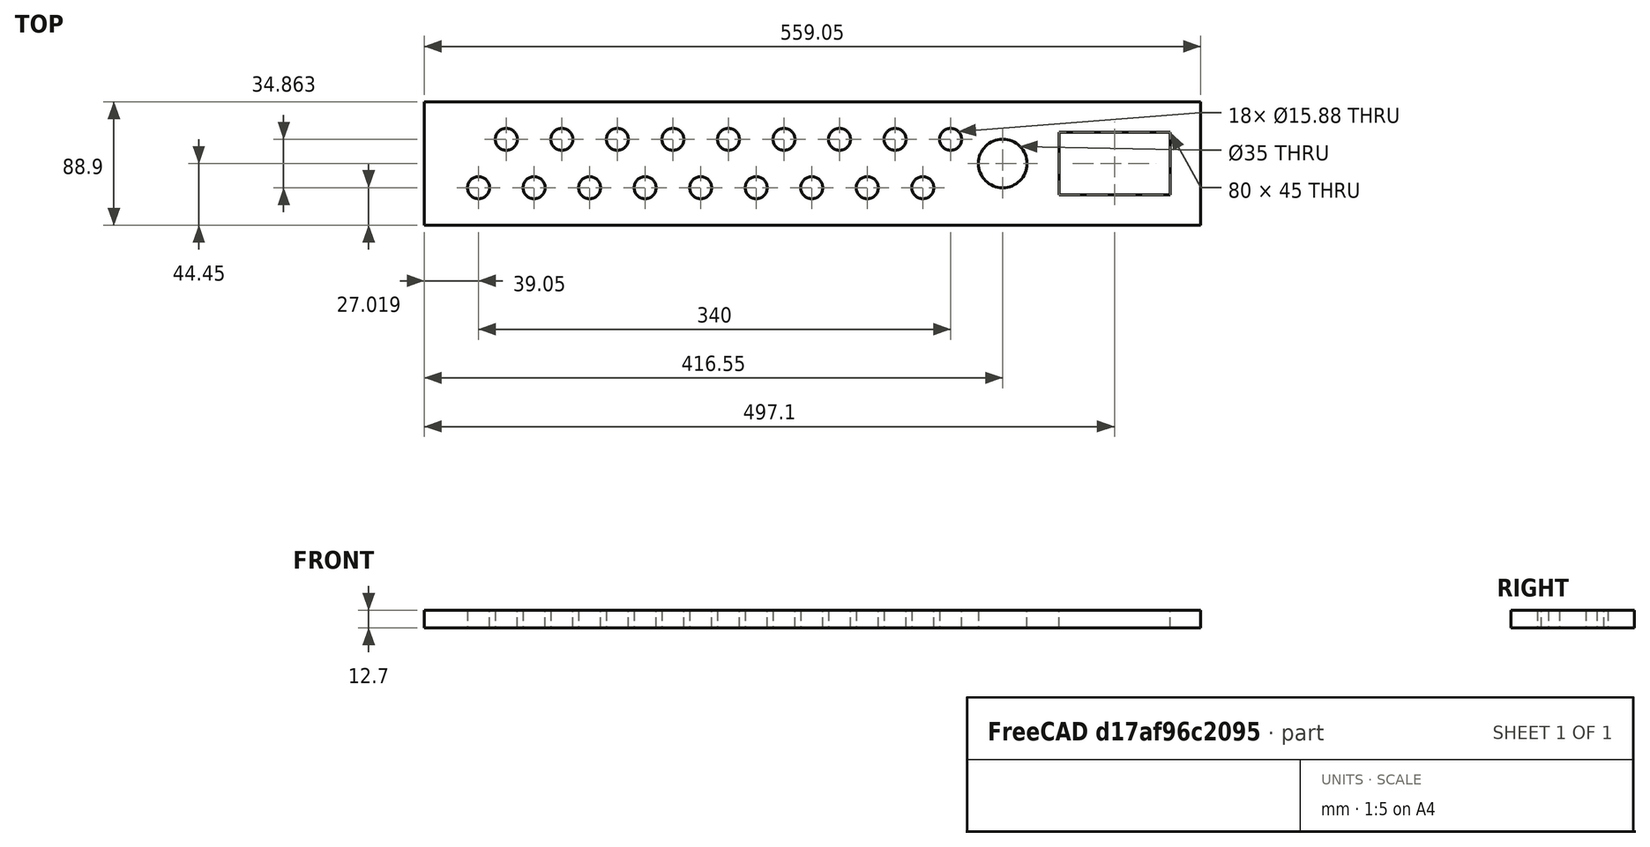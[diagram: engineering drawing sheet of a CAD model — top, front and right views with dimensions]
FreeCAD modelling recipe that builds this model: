
FCSTD DOCUMENT  (FreeCAD 0.19R24291 (Git))
Label: top3
License: All rights reserved
LicenseURL: http://en.wikipedia.org/wiki/All_rights_reserved
objects: TechDraw::DrawViewDimension×14, Sketcher::SketchObject×1, PartDesign::Pad×1, PartDesign::Body×1, TechDraw::DrawSVGTemplate×1, TechDraw::DrawViewPart×1, TechDraw::DrawPage×1
note: 4 computed .brp shape members not serialized (recipe doc carries the construction recipe); baked Part::Feature solids carry a one-line shape summary decoded from their .brp

FEATURE [Sketcher::SketchObject] Sketch
  FullyConstrained = true
  MapMode = 5
  Support = -> [XY_Plane]
  expr: Constraints[34] = (3.5 * 25.4 - 2 * 5 / 8 * 25.4) / 3 + 5 / 8 * 25.5 / 2
  expr: Constraints[0] = 5 / 8 * 25.4
  expr: Constraints[26] = 3.5 * 25.4
  expr: Constraints[38] = 20 + 20
  expr: Constraints[53] = (3.5 * 25.4 - 2 * 5 / 8 * 25.4) / 3 + 5 / 8 * 25.5 / 2
  expr: Constraints[103] = 3 / 4 * 25.4
  sketch-geometry (35):
    g0: Circle CenterX=20 CenterY=27.0187 CenterZ=0 NormalX=0 NormalY=0 NormalZ=1 AngleXU=0 Radius=7.9375
    g1: LineSegment StartX=-2e-16 StartY=27.0187 StartZ=0 EndX=380 EndY=27.0187 EndZ=0
    g2: Circle CenterX=60 CenterY=27.0187 CenterZ=0 NormalX=0 NormalY=0 NormalZ=1 AngleXU=0 Radius=7.9375
    g3: Circle CenterX=397.5 CenterY=44.45 CenterZ=0 NormalX=0 NormalY=0 NormalZ=1 AngleXU=0 Radius=17.5
    g4: LineSegment StartX=438.05 StartY=66.95 StartZ=0 EndX=518.05 EndY=66.95 EndZ=0
    g5: LineSegment StartX=518.05 StartY=66.95 StartZ=0 EndX=518.05 EndY=21.95 EndZ=0
    g6: LineSegment StartX=518.05 StartY=21.95 StartZ=0 EndX=438.05 EndY=21.95 EndZ=0
    g7: LineSegment StartX=438.05 StartY=21.95 StartZ=0 EndX=438.05 EndY=66.95 EndZ=0
    g8: LineSegment StartX=0 StartY=88.9 StartZ=0 EndX=540 EndY=88.9 EndZ=0
    g9: LineSegment StartX=540 StartY=88.9 StartZ=0 EndX=540 EndY=0 EndZ=0
    g10: LineSegment StartX=540 StartY=0 StartZ=0 EndX=0 EndY=0 EndZ=0
    g11: LineSegment StartX=0 StartY=0 StartZ=0 EndX=0 EndY=88.9 EndZ=0
    g12: LineSegment StartX=540 StartY=44.45 StartZ=0 EndX=0 EndY=44.45 EndZ=0
    g13: GeomPoint X=518.05 Y=44.45 Z=0
    g14: LineSegment StartX=0 StartY=61.8812 StartZ=0 EndX=380 EndY=61.8812 EndZ=0
    g15: Circle CenterX=40 CenterY=61.8812 CenterZ=0 NormalX=0 NormalY=0 NormalZ=1 AngleXU=0 Radius=7.9375
    g16: Circle CenterX=100 CenterY=27.0187 CenterZ=0 NormalX=0 NormalY=0 NormalZ=1 AngleXU=0 Radius=7.9375
    g17: Circle CenterX=140 CenterY=27.0187 CenterZ=0 NormalX=0 NormalY=0 NormalZ=1 AngleXU=0 Radius=7.9375
    g18: Circle CenterX=180 CenterY=27.0187 CenterZ=0 NormalX=0 NormalY=0 NormalZ=1 AngleXU=0 Radius=7.9375
    g19: Circle CenterX=220 CenterY=27.0187 CenterZ=0 NormalX=0 NormalY=0 NormalZ=1 AngleXU=0 Radius=7.9375
    g20: Circle CenterX=260 CenterY=27.0187 CenterZ=0 NormalX=0 NormalY=0 NormalZ=1 AngleXU=0 Radius=7.9375
    g21: Circle CenterX=300 CenterY=27.0187 CenterZ=0 NormalX=0 NormalY=0 NormalZ=1 AngleXU=0 Radius=7.9375
    g22: Circle CenterX=340 CenterY=27.0187 CenterZ=0 NormalX=0 NormalY=0 NormalZ=1 AngleXU=0 Radius=7.9375
    g23: Circle CenterX=80 CenterY=61.8812 CenterZ=0 NormalX=0 NormalY=0 NormalZ=1 AngleXU=0 Radius=7.9375
    g24: Circle CenterX=120 CenterY=61.8812 CenterZ=0 NormalX=0 NormalY=0 NormalZ=1 AngleXU=0 Radius=7.9375
    g25: Circle CenterX=160 CenterY=61.8812 CenterZ=0 NormalX=0 NormalY=0 NormalZ=1 AngleXU=0 Radius=7.9375
    g26: Circle CenterX=200 CenterY=61.8812 CenterZ=0 NormalX=0 NormalY=0 NormalZ=1 AngleXU=0 Radius=7.9375
    g27: Circle CenterX=240 CenterY=61.8812 CenterZ=0 NormalX=0 NormalY=0 NormalZ=1 AngleXU=0 Radius=7.9375
    g28: Circle CenterX=280 CenterY=61.8812 CenterZ=0 NormalX=0 NormalY=0 NormalZ=1 AngleXU=0 Radius=7.9375
    g29: Circle CenterX=320 CenterY=61.8812 CenterZ=0 NormalX=0 NormalY=0 NormalZ=1 AngleXU=0 Radius=7.9375
    g30: Circle CenterX=360 CenterY=61.8812 CenterZ=0 NormalX=0 NormalY=0 NormalZ=1 AngleXU=0 Radius=7.9375
    g31: LineSegment StartX=380 StartY=0 StartZ=0 EndX=380 EndY=88.9 EndZ=0
    g32: LineSegment StartX=0 StartY=0 StartZ=0 EndX=-19.05 EndY=0 EndZ=0
    g33: LineSegment StartX=-19.05 StartY=0 StartZ=0 EndX=-19.05 EndY=88.9 EndZ=0
    g34: LineSegment StartX=-19.05 StartY=88.9 StartZ=0 EndX=0 EndY=88.9 EndZ=0
  constraints (105):
    c: Diameter(g0) = 15.875
    c: Horizontal(g1)
    c: PointOnObject(g0,g1)
    c: DistanceX(g1,g0) = 20
    c: Equal(g0,g2) = 15.875
    c: PointOnObject(g2,g1)
    c: DistanceX(g0,g2) = 40
    c: Diameter(g3) = 35
    c: Coincident(g4,g5)
    c: Coincident(g5,g6)
    c: Coincident(g6,g7)
    c: Coincident(g7,g4)
    c: Horizontal(g4)
    c: Horizontal(g6)
    c: Vertical(g5)
    c: Vertical(g7)
    c: DistanceX(g6,g6) = 80
    c: DistanceY(g5,g5) = 45
    c: Coincident(g8,g9)
    c: Coincident(g9,g10)
    c: Coincident(g10,g11)
    c: Coincident(g11,g8)
    c: Horizontal(g8)
    c: Horizontal(g10)
    c: Vertical(g9)
    c: Vertical(g11)
    c: DistanceY(g11,g11) = 88.9
    c: Coincident(g10,g-1)
    c: Horizontal(g12)
    c: Symmetric(g8,g9,g12)
    c: Symmetric(g4,g5,g13)
    c: PointOnObject(g13,g12)
    c: PointOnObject(g3,g12)
    c: PointOnObject(g1,g11)
    c: DistanceY(g10,g1) = 27.0187
    c: Horizontal(g14)
    c: PointOnObject(g14,g11)
    c: PointOnObject(g15,g14)
    c: DistanceX(g14,g15) = 40
    c: Equal(g0,g16) = 15.875
    c: PointOnObject(g16,g1)
    c: Equal(g0,g17) = 15.875
    c: PointOnObject(g17,g1)
    c: Equal(g0,g18) = 15.875
    c: PointOnObject(g18,g1)
    c: Equal(g0,g19) = 15.875
    c: PointOnObject(g19,g1)
    c: Equal(g0,g20) = 15.875
    c: PointOnObject(g20,g1)
    c: Equal(g0,g21) = 15.875
    c: PointOnObject(g21,g1)
    c: Equal(g0,g22) = 15.875
    c: PointOnObject(g22,g1)
    c: DistanceY(g14,g8) = 27.0187
    c: Equal(g0,g23) = 15.875
    c: PointOnObject(g23,g14)
    c: Equal(g0,g24) = 15.875
    c: PointOnObject(g24,g14)
    c: Equal(g0,g25) = 15.875
    c: PointOnObject(g25,g14)
    c: Equal(g0,g26) = 15.875
    c: PointOnObject(g26,g14)
    c: Equal(g0,g27) = 15.875
    c: PointOnObject(g27,g14)
    c: Equal(g0,g28) = 15.875
    c: PointOnObject(g28,g14)
    c: Equal(g0,g29) = 15.875
    c: PointOnObject(g29,g14)
    c: Equal(g0,g30) = 15.875
    c: PointOnObject(g30,g14)
    c: PointOnObject(g31,g10)
    c: PointOnObject(g31,g8)
    c: Vertical(g31)
    c: PointOnObject(g14,g31)
    c: PointOnObject(g1,g31)
    c: DistanceX(g15,g23) = 40
    c: DistanceX(g23,g24) = 40
    c: DistanceX(g24,g25) = 40
    c: DistanceX(g25,g26) = 40
    c: DistanceX(g26,g27) = 40
    c: DistanceX(g27,g28) = 40
    c: DistanceX(g28,g29) = 40
    c: DistanceX(g29,g30) = 40
    c: PointOnObject(g12,g11)
    c: Equal(g15,g0)
    c: DistanceX(g2,g16) = 40
    c: DistanceX(g16,g17) = 40
    c: DistanceX(g17,g18) = 40
    c: DistanceX(g18,g19) = 40
    c: DistanceX(g19,g20) = 40
    c: DistanceX(g20,g21) = 40
    c: DistanceX(g21,g22) = 40
    c: DistanceX(g30,g14) = 20
    c: Tangent(g3,g31)
    c: DistanceY(g4,g8) = 21.95
    c: DistanceX(g13,g12) = 21.95
    c: Coincident(g10,g32)
    c: PointOnObject(g32,g-1)
    c: Coincident(g32,g33)
    c: Vertical(g33)
    c: Coincident(g33,g34)
    c: Coincident(g34,g8)
    c: Horizontal(g34)
    c: DistanceX(g32,g10) = 19.05
    c: DistanceX(g10,g9) = 540
FEATURE [PartDesign::Pad] Pad
  Direction = (1,1,1)
  Length = 12.7
  Length2 = 100
  Profile = -> Sketch
  Type = 0
  expr: Length = 1 / 2 * 25.4
FEATURE [PartDesign::Body] Body
  Group = -> [Sketch,Pad]
  Origin = -> Origin
  Tip = -> Pad
FEATURE [TechDraw::DrawSVGTemplate] Template
  EditableTexts = Designed_by_Name=Designed by Name; Drawing_number=Drawing number; FC-Date=Date; FC-SC=Scale; FC-SH=Sheet; FC-Title=Title; Subtitle=Subtitle; Weight=Weight
  Height = 210
  Orientation = 1
  Width = 297
FEATURE [TechDraw::DrawViewPart] View
  CoarseView = false
  Direction = (0,0,1)
  Focus = 100
  HardHidden = false
  IsoCount = 0
  IsoHidden = false
  IsoVisible = false
  LockPosition = false
  Perspective = false
  Rotation = 0
  Scale = 0.4
  ScaleType = 0
  SeamHidden = false
  SeamVisible = true
  SmoothHidden = false
  SmoothVisible = true
  Source = -> [Body]
  X = 148.5
  XDirection = (1,0,0)
  Y = 105
FEATURE [TechDraw::DrawViewDimension] Dimension
  Arbitrary = false
  ArbitraryTolerances = false
  EqualTolerance = true
  FormatSpec = %.2f
  FormatSpecOverTolerance = %+.2f
  FormatSpecUnderTolerance = %+.2f
  Inverted = false
  LockPosition = false
  MeasureType = 1
  OverTolerance = 0
  References2D = -> [View]
  Rotation = 0
  ScaleType = 0
  TheoreticalExact = false
  Type = 2
  UnderTolerance = 0
  X = -136.054
  Y = 3.66279
FEATURE [TechDraw::DrawViewDimension] Dimension001
  Arbitrary = false
  ArbitraryTolerances = false
  EqualTolerance = true
  FormatSpec = %.2f
  FormatSpecOverTolerance = %+.2f
  FormatSpecUnderTolerance = %+.2f
  Inverted = false
  LockPosition = false
  MeasureType = 1
  OverTolerance = 0
  References2D = -> [View]
  Rotation = 0
  ScaleType = 0
  TheoreticalExact = false
  Type = 1
  UnderTolerance = 0
  X = -5.75581
  Y = 69.5823
FEATURE [TechDraw::DrawViewDimension] Dimension002
  Arbitrary = false
  ArbitraryTolerances = false
  EqualTolerance = true
  FormatSpec = %.2f
  FormatSpecOverTolerance = %+.2f
  FormatSpecUnderTolerance = %+.2f
  Inverted = false
  LockPosition = false
  MeasureType = 1
  OverTolerance = 0
  References2D = -> [View]
  Rotation = 0
  ScaleType = 0
  TheoreticalExact = false
  Type = 1
  UnderTolerance = 0
  X = -103.826
  Y = -32.6088
FEATURE [TechDraw::DrawViewDimension] Dimension003
  Arbitrary = false
  ArbitraryTolerances = false
  EqualTolerance = true
  FormatSpec = %.2f
  FormatSpecOverTolerance = %+.2f
  FormatSpecUnderTolerance = %+.2f
  Inverted = false
  LockPosition = false
  MeasureType = 1
  OverTolerance = 0
  References2D = -> [View]
  Rotation = 0
  ScaleType = 0
  TheoreticalExact = false
  Type = 1
  UnderTolerance = 0
  X = -88.7133
  Y = -33.1353
FEATURE [TechDraw::DrawViewDimension] Dimension004
  Arbitrary = false
  ArbitraryTolerances = false
  EqualTolerance = true
  FormatSpec = %.2f
  FormatSpecOverTolerance = %+.2f
  FormatSpecUnderTolerance = %+.2f
  Inverted = false
  LockPosition = false
  MeasureType = 1
  OverTolerance = 0
  References2D = -> [View]
  Rotation = 0
  ScaleType = 0
  TheoreticalExact = false
  Type = 1
  UnderTolerance = 0
  X = -100.349
  Y = 35.0507
FEATURE [TechDraw::DrawViewDimension] Dimension005
  Arbitrary = false
  ArbitraryTolerances = false
  EqualTolerance = true
  FormatSpec = %.2f
  FormatSpecOverTolerance = %+.2f
  FormatSpecUnderTolerance = %+.2f
  Inverted = false
  LockPosition = false
  MeasureType = 1
  OverTolerance = 0
  References2D = -> [View]
  Rotation = 0
  ScaleType = 0
  TheoreticalExact = false
  Type = 2
  UnderTolerance = 0
  X = -122.837
  Y = -32.4344
FEATURE [TechDraw::DrawViewDimension] Dimension006
  Arbitrary = false
  ArbitraryTolerances = false
  EqualTolerance = true
  FormatSpec = %.2f
  FormatSpecOverTolerance = %+.2f
  FormatSpecUnderTolerance = %+.2f
  Inverted = false
  LockPosition = false
  MeasureType = 1
  OverTolerance = 0
  References2D = -> [View]
  Rotation = 0
  ScaleType = 0
  TheoreticalExact = false
  Type = 2
  UnderTolerance = 0
  X = -128.605
  Y = -7.67119
FEATURE [TechDraw::DrawViewDimension] Dimension007
  Arbitrary = false
  ArbitraryTolerances = false
  EqualTolerance = true
  FormatSpec = %.2f
  FormatSpecOverTolerance = %+.2f
  FormatSpecUnderTolerance = %+.2f
  Inverted = false
  LockPosition = false
  MeasureType = 1
  OverTolerance = 0
  References2D = -> [View]
  Rotation = 0
  ScaleType = 0
  TheoreticalExact = false
  Type = 1
  UnderTolerance = 0
  X = 82.4379
  Y = -32.2621
FEATURE [TechDraw::DrawViewDimension] Dimension008
  Arbitrary = false
  ArbitraryTolerances = false
  EqualTolerance = true
  FormatSpec = %.2f
  FormatSpecOverTolerance = %+.2f
  FormatSpecUnderTolerance = %+.2f
  Inverted = false
  LockPosition = false
  MeasureType = 1
  OverTolerance = 0
  References2D = -> [View]
  Rotation = 0
  ScaleType = 0
  TheoreticalExact = false
  Type = 2
  UnderTolerance = 0
  X = 43.1937
  Y = -34.3551
FEATURE [TechDraw::DrawViewDimension] Dimension009
  Arbitrary = false
  ArbitraryTolerances = false
  EqualTolerance = true
  FormatSpec = %.2f
  FormatSpecOverTolerance = %+.2f
  FormatSpecUnderTolerance = %+.2f
  Inverted = false
  LockPosition = false
  MeasureType = 1
  OverTolerance = 0
  References2D = -> [View]
  Rotation = 0
  ScaleType = 0
  TheoreticalExact = false
  Type = 1
  UnderTolerance = 0
  X = 87.3619
  Y = 43.7388
FEATURE [TechDraw::DrawViewDimension] Dimension010
  Arbitrary = false
  ArbitraryTolerances = false
  EqualTolerance = true
  FormatSpec = %.2f
  FormatSpecOverTolerance = %+.2f
  FormatSpecUnderTolerance = %+.2f
  Inverted = false
  LockPosition = false
  MeasureType = 1
  OverTolerance = 0
  References2D = -> [View]
  Rotation = 0
  ScaleType = 0
  TheoreticalExact = false
  Type = 2
  UnderTolerance = 0
  X = 122.42
  Y = 29.0877
FEATURE [TechDraw::DrawViewDimension] Dimension011
  Arbitrary = false
  ArbitraryTolerances = false
  EqualTolerance = true
  FormatSpec = %.2f
  FormatSpecOverTolerance = %+.2f
  FormatSpecUnderTolerance = %+.2f
  Inverted = false
  LockPosition = false
  MeasureType = 1
  OverTolerance = 0
  References2D = -> [View]
  Rotation = 0
  ScaleType = 0
  TheoreticalExact = false
  Type = 1
  UnderTolerance = 0
  X = 56.3619
  Y = 40.5993
FEATURE [TechDraw::DrawViewDimension] Dimension012
  Arbitrary = false
  ArbitraryTolerances = false
  EqualTolerance = true
  FormatSpec = ⌀%.2f
  FormatSpecOverTolerance = %+.2f
  FormatSpecUnderTolerance = %+.2f
  Inverted = false
  LockPosition = false
  MeasureType = 1
  OverTolerance = 0
  References2D = -> [View]
  Rotation = 0
  ScaleType = 0
  TheoreticalExact = false
  Type = 5
  UnderTolerance = 0
  X = -73.2558
  Y = 28.6047
FEATURE [TechDraw::DrawViewDimension] Dimension013
  Arbitrary = false
  ArbitraryTolerances = false
  EqualTolerance = true
  FormatSpec = ⌀%.2f
  FormatSpecOverTolerance = %+.2f
  FormatSpecUnderTolerance = %+.2f
  Inverted = false
  LockPosition = false
  MeasureType = 1
  OverTolerance = 0
  References2D = -> [View]
  Rotation = 0
  ScaleType = 0
  TheoreticalExact = false
  Type = 5
  UnderTolerance = 0
  X = 44.3023
  Y = 30.6977
FEATURE [TechDraw::DrawPage] Page
  KeepUpdated = true
  NextBalloonIndex = 1
  ProjectionType = 0
  Template = -> Template
  Views = -> [View,Dimension,Dimension001,Dimension002,Dimension003,Dimension004,Dimension005,Dimension006,Dimension007,Dimension008,Dimension009,Dimension010,Dimension011,Dimension012,Dimension013]
